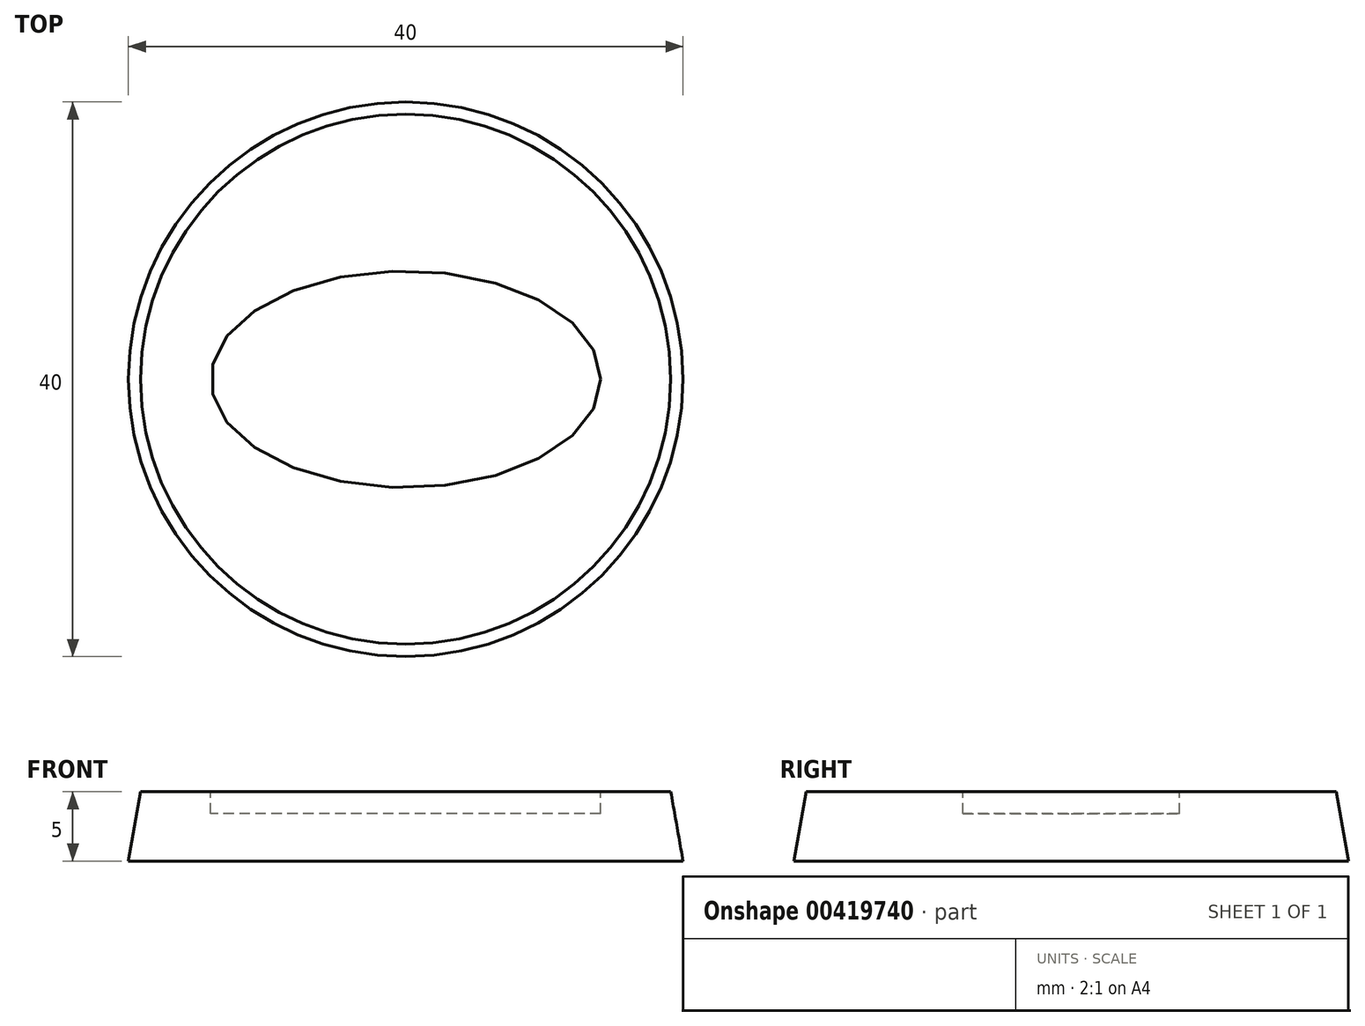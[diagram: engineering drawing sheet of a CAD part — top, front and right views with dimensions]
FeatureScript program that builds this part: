
annotation { "Feature Type Name" : "Feature", "Feature Type Description" : "" }
export const myFeature = defineFeature(function(context is Context, id is Id, definition is map)
    precondition{}
    {
        {
            var Q0;
            Q0=qCreatedBy(makeId("Top.planeOp"),FACE);
            var sketch = newSketch(context, id + "F0", { "sketchPlane" : qUnion([Q0])});
            skCircle(sketch, "E0", {"center": v(0, 0) * mm, "radius": 20 * mm});
            skSolve(sketch);
        }
        {
            var Q0;
            Q0=makeQuery(id+"F0.imprint","IMPRINT",FACE,{"disambiguationData":[TD([[makeQuery(id+"F0.imprint","IMPRINT",EDGE,{"derivedFrom":sQuery(id+"F0.wireOp",EDGE,"E0")}),1.0]])]});
            extrude(context, id + "F1", {"entities" : qUnion([Q0]), "oppositeDirection" : true, "depth" : 5 * mm});
        }
        {
            var Q0;
            Q0=makeQuery(id+"F1.opExtrude","CAP_EDGE",EDGE,{"disambiguationData":[OSD([sQuery(id+"F0.wireOp",EDGE,"E0")])],"isStart":true});
            chamfer(context, id + "F2", {"entities" : qUnion([Q0]), "chamferType" : ChamferType.OFFSET_ANGLE, "width" : 5 * mm, "oppositeDirection" : true, "angle" : 10 * degree, "tangentPropagation" : true});
        }
        {
            var Q0;
            Q0=makeQuery(id+"F1.opExtrude","CAP_FACE",FACE,{"disambiguationData":[OSD([sQuery(id+"F0.wireOp",EDGE,"E0")])],"isStart":true});
            var sketch = newSketch(context, id + "F3", { "sketchPlane" : qUnion([Q0])});
            skEllipse(sketch, "E1", {"center": v(0, 0) * mm, "majorRadius": 14.06 * mm, "minorRadius": 7.81 * mm, "majorAxis": v(1, 0)});
            skSolve(sketch);
        }
        {
            var Q0;
            Q0=makeQuery(id+"F3.imprint","IMPRINT",FACE,{"disambiguationData":[TD([[makeQuery(id+"F3.imprint","IMPRINT",EDGE,{"derivedFrom":sQuery(id+"F3.wireOp",EDGE,"E1")}),1.0]])]});
            extrude(context, id + "F4", {"entities" : qUnion([Q0]), "operationType" : NewBodyOperationType.REMOVE, "oppositeDirection" : true, "depth" : 1.57 * mm});
        }
    });
